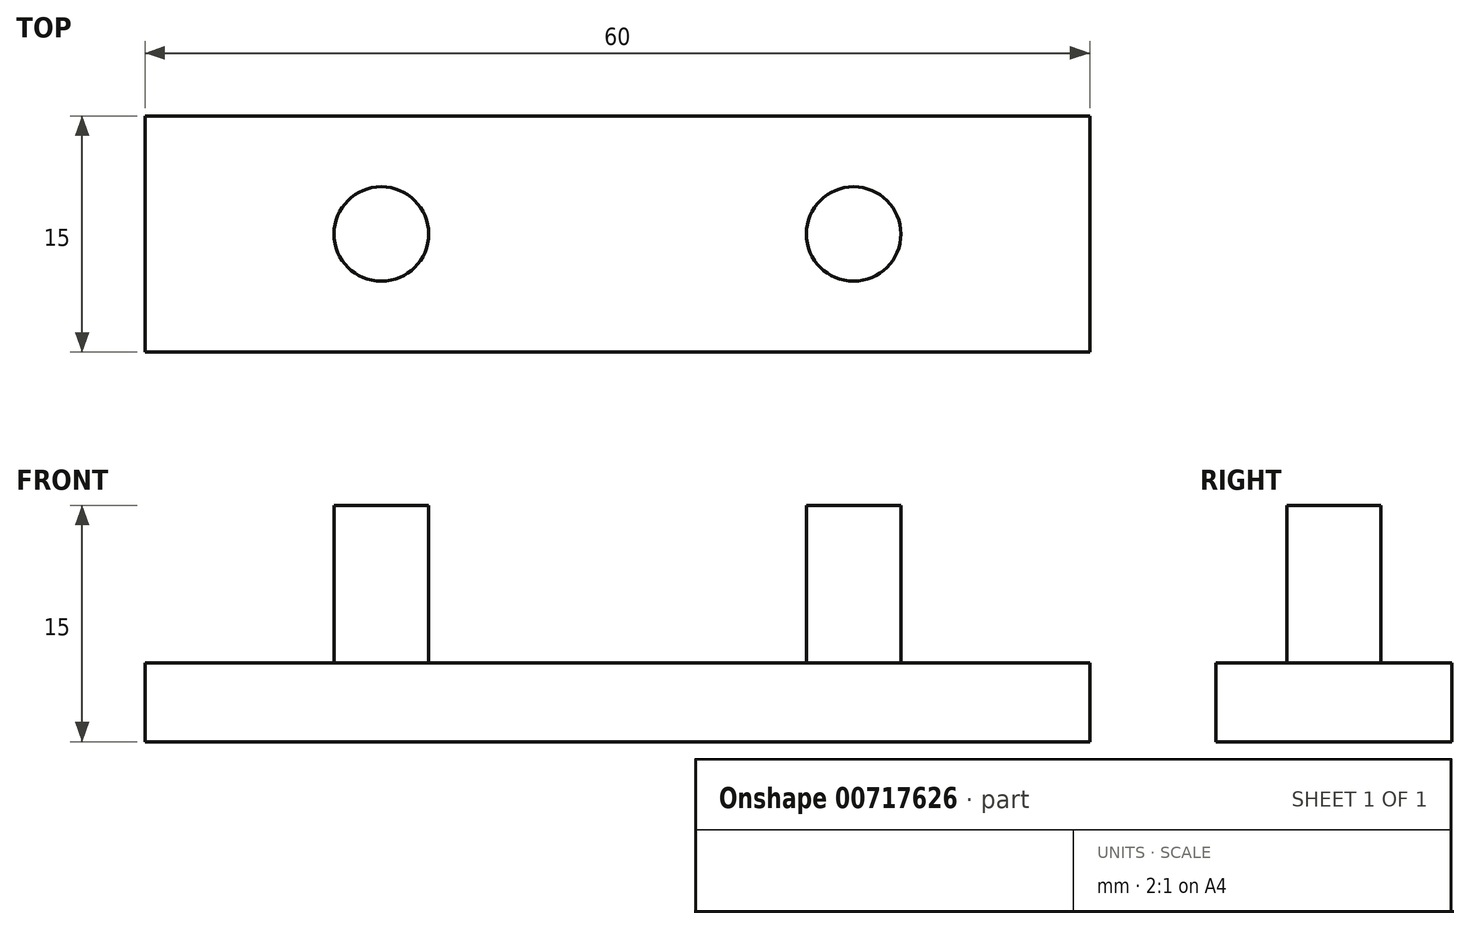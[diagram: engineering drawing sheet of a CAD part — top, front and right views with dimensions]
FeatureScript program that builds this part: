
annotation { "Feature Type Name" : "Feature", "Feature Type Description" : "" }
export const myFeature = defineFeature(function(context is Context, id is Id, definition is map)
    precondition{}
    {
        {
            var Q0;
            Q0=qCreatedBy(makeId("Top.planeOp"),FACE);
            var sketch = newSketch(context, id + "F0", { "sketchPlane" : qUnion([Q0])});
            skLineSegment(sketch, "E0.bottom", {"start": v(30, -7.5) * mm, "end": v(-30, -7.5) * mm});
            skLineSegment(sketch, "E0.top", {"start": v(30, 7.5) * mm, "end": v(-30, 7.5) * mm});
            skLineSegment(sketch, "E0.left", {"start": v(30, -7.5) * mm, "end": v(30, 7.5) * mm});
            skLineSegment(sketch, "E0.right", {"start": v(-30, -7.5) * mm, "end": v(-30, 7.5) * mm});
            skPoint(sketch, "E0.middle", {"position": v(0, 0) * mm});
            skSolve(sketch);
        }
        {
            var Q0;
            Q0 = qSketchRegion(id + "F0", true);
            extrude(context, id + "F1", {"entities" : qUnion([Q0]), "depth" : 5 * mm, "offsetDistance" : 25 * mm});
        }
        {
            var Q0;
            Q0=makeQuery(id+"F1.opExtrude","CAP_FACE",FACE,{"disambiguationData":[OSD([sQuery(id+"F0.wireOp",EDGE,"E0.bottom"),sQuery(id+"F0.wireOp",EDGE,"E0.top"),sQuery(id+"F0.wireOp",EDGE,"E0.left"),sQuery(id+"F0.wireOp",EDGE,"E0.right")])],"isStart":false});
            var sketch = newSketch(context, id + "F2", { "sketchPlane" : qUnion([Q0])});
            skPoint(sketch, "E1", {"position": v(-15, 0) * mm});
            skPoint(sketch, "E2", {"position": v(15, 0) * mm});
            skCircle(sketch, "E3", {"center": v(-15, 0) * mm, "radius": 3 * mm});
            skCircle(sketch, "E4", {"center": v(15, 0) * mm, "radius": 3 * mm});
            skSolve(sketch);
        }
        {
            var Q0;
            Q0=makeQuery(id+"F2.imprint","IMPRINT",FACE,{"disambiguationData":[TD([[makeQuery(id+"F2.imprint","IMPRINT",EDGE,{"derivedFrom":sQuery(id+"F2.wireOp",EDGE,"E3")}),1.0]])]});
            var Q1;
            Q1=makeQuery(id+"F2.imprint","IMPRINT",FACE,{"disambiguationData":[TD([[makeQuery(id+"F2.imprint","IMPRINT",EDGE,{"derivedFrom":sQuery(id+"F2.wireOp",EDGE,"E4")}),1.0]])]});
            extrude(context, id + "F3", {"entities" : qUnion([Q0, Q1]), "operationType" : NewBodyOperationType.ADD, "depth" : 10 * mm, "offsetDistance" : 25 * mm});
        }
    });
